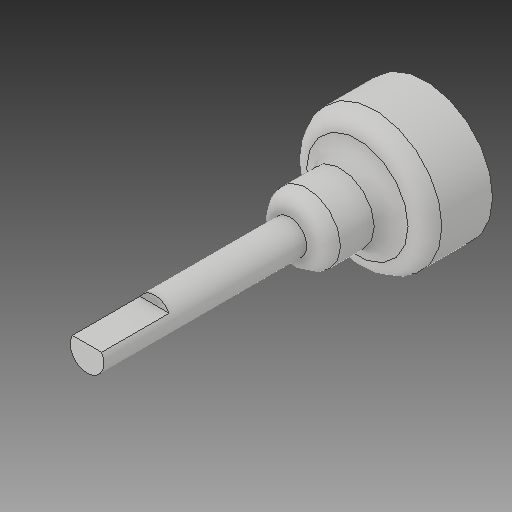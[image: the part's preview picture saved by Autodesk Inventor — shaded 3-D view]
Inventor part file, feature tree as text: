
AUTODESK INVENTOR PART (.ipt)
format: ipt  version: 2017 (Build 210142000, 142)  size: 164,864 bytes
history: native  units: in
note: dims shown in document units (in); Inventor stores cm internally (conversion verified against a paired STEP export)
features: sketch x6, extrude x5, fillet x3, thicken_offset x2, hole x1, plane x1
ambient origin geometry x8: Origin, YZ Plane, XZ Plane, XY Plane, X Axis, Y Axis, Z Axis, Center Point
bodies: Solid1 (feature_tree)
feature tree (18):
  sketch  "Sketch1"  dims[d0=1.0in d1=0.5in]
  extrude  "Extrusion1"  Depth=0.5in
  extrude  "Extrusion2"  Depth=1.0in TaperAngle=0.0deg
  fillet  "Fillet1"  Radius=0.125in
  fillet  "Fillet2"  Radius=0.125in
  extrude  "Extrusion3"  Depth=0.25in TaperAngle=0.0deg
  extrude  "Extrusion4"  Depth=0.125in TaperAngle=0.0deg
  fillet  "Fillet3"  Radius=0.125in
  extrude  "Extrusion6"  Depth=0.0625in TaperAngle=0.0deg
  hole  "Hole1"  [1 undecoded]
  sketch  "Sketch8"  dims[d23=0.125in d24=0.75in d25=0.375in d26=0.25in d27=0.5635in d28=1.0in d29=0.8108in d32=0.15in d35=9.0in d36=9.0in d37=5.0in d38=5.0in]
  plane  "Work Plane3"
  thicken_offset  "Thicken1"
  thicken_offset  "Thicken2"
  sketch  "Sketch3"  dims[d2=0.5in d3=0.0in d4=1.0in d5=0.0in d6=0.125in d7=0.125in]
  sketch  "Sketch4"  dims[d8=0.25in d9=10.5in d10=0.0in]
  sketch  "Sketch6"  dims[d11=0.0625in d12=4.5in d13=0.0in d17=0.125in]
  sketch  "Sketch7"  dims[d18=0.1875in d19=0.0625in d20=0.0in]
note: 1 required parameter value undecoded (feature->parameter linkage not recoverable at this tier; creation-order binding heuristic only, values carry confidence <= 0.55)
